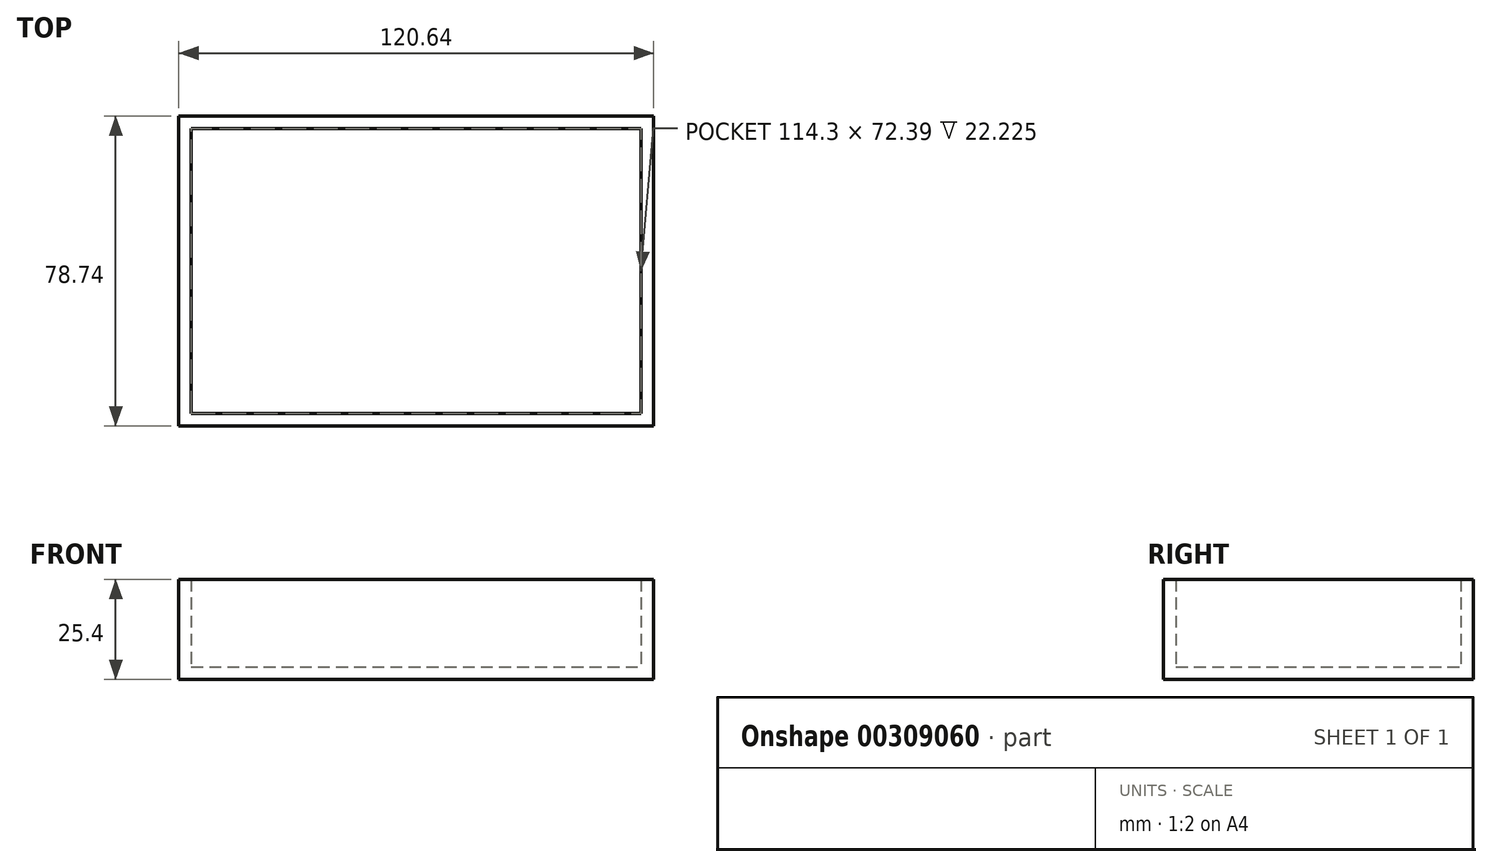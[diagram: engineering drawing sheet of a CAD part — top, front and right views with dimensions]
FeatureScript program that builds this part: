
annotation { "Feature Type Name" : "Feature", "Feature Type Description" : "" }
export const myFeature = defineFeature(function(context is Context, id is Id, definition is map)
    precondition{}
    {
        {
            var Q0;
            Q0=qCreatedBy(makeId("Top.planeOp"),FACE);
            var sketch = newSketch(context, id + "F0", { "sketchPlane" : qUnion([Q0])});
            skLineSegment(sketch, "E0.bottom", {"start": v(-60.33, -39.37) * mm, "end": v(60.32, -39.37) * mm});
            skLineSegment(sketch, "E0.top", {"start": v(-60.33, 39.37) * mm, "end": v(60.33, 39.37) * mm});
            skLineSegment(sketch, "E0.left", {"start": v(-60.33, -39.37) * mm, "end": v(-60.33, 39.37) * mm});
            skLineSegment(sketch, "E0.right", {"start": v(60.33, -39.37) * mm, "end": v(60.33, 39.37) * mm});
            skPoint(sketch, "E0.middle", {"position": v(0, 0) * mm});
            skPoint(sketch, "E1", {"position": v(-43.18, 24.13) * mm});
            skPoint(sketch, "E2", {"position": v(31.75, 24.13) * mm});
            skPoint(sketch, "E3", {"position": v(31.75, -24.13) * mm});
            skPoint(sketch, "E4", {"position": v(-43.18, -24.13) * mm});
            skPoint(sketch, "E5", {"position": v(7.62, 8.9) * mm});
            skPoint(sketch, "E6", {"position": v(7.62, -19.05) * mm});
            skSolve(sketch);
        }
        {
            var Q0;
            Q0 = qSketchRegion(id + "F0", true);
            extrude(context, id + "F1", {"entities" : qUnion([Q0]), "depth" : 3.17 * mm});
        }
        {
            var Q0;
            Q0=makeQuery(id+"F1.opExtrude","CAP_FACE",FACE,{"disambiguationData":[OSD([sQuery(id+"F0.wireOp",EDGE,"E0.bottom"),sQuery(id+"F0.wireOp",EDGE,"E0.top"),sQuery(id+"F0.wireOp",EDGE,"E0.left"),sQuery(id+"F0.wireOp",EDGE,"E0.right")])],"isStart":false});
            var sketch = newSketch(context, id + "F2", { "sketchPlane" : qUnion([Q0])});
            skLineSegment(sketch, "E7.0", {"start": v(-57.15, 36.2) * mm, "end": v(57.15, 36.2) * mm});
            skLineSegment(sketch, "E7.1", {"start": v(-57.15, -36.2) * mm, "end": v(-57.15, 36.2) * mm});
            skLineSegment(sketch, "E7.2", {"start": v(-57.15, -36.2) * mm, "end": v(57.15, -36.2) * mm});
            skLineSegment(sketch, "E7.3", {"start": v(57.15, -36.2) * mm, "end": v(57.15, 36.2) * mm});
            skSolve(sketch);
        }
        {
            var Q0;
            Q0=makeQuery(id+"F2.imprint","IMPRINT",FACE,{"disambiguationData":[TD([[makeQuery(id+"F2.imprint","IMPRINT",EDGE,{"derivedFrom":sQuery(id+"F2.wireOp",EDGE,"E7.0")}),1.0]])]});
            extrude(context, id + "F3", {"entities" : qUnion([Q0]), "operationType" : NewBodyOperationType.ADD, "depth" : 22.22 * mm});
        }
    });
